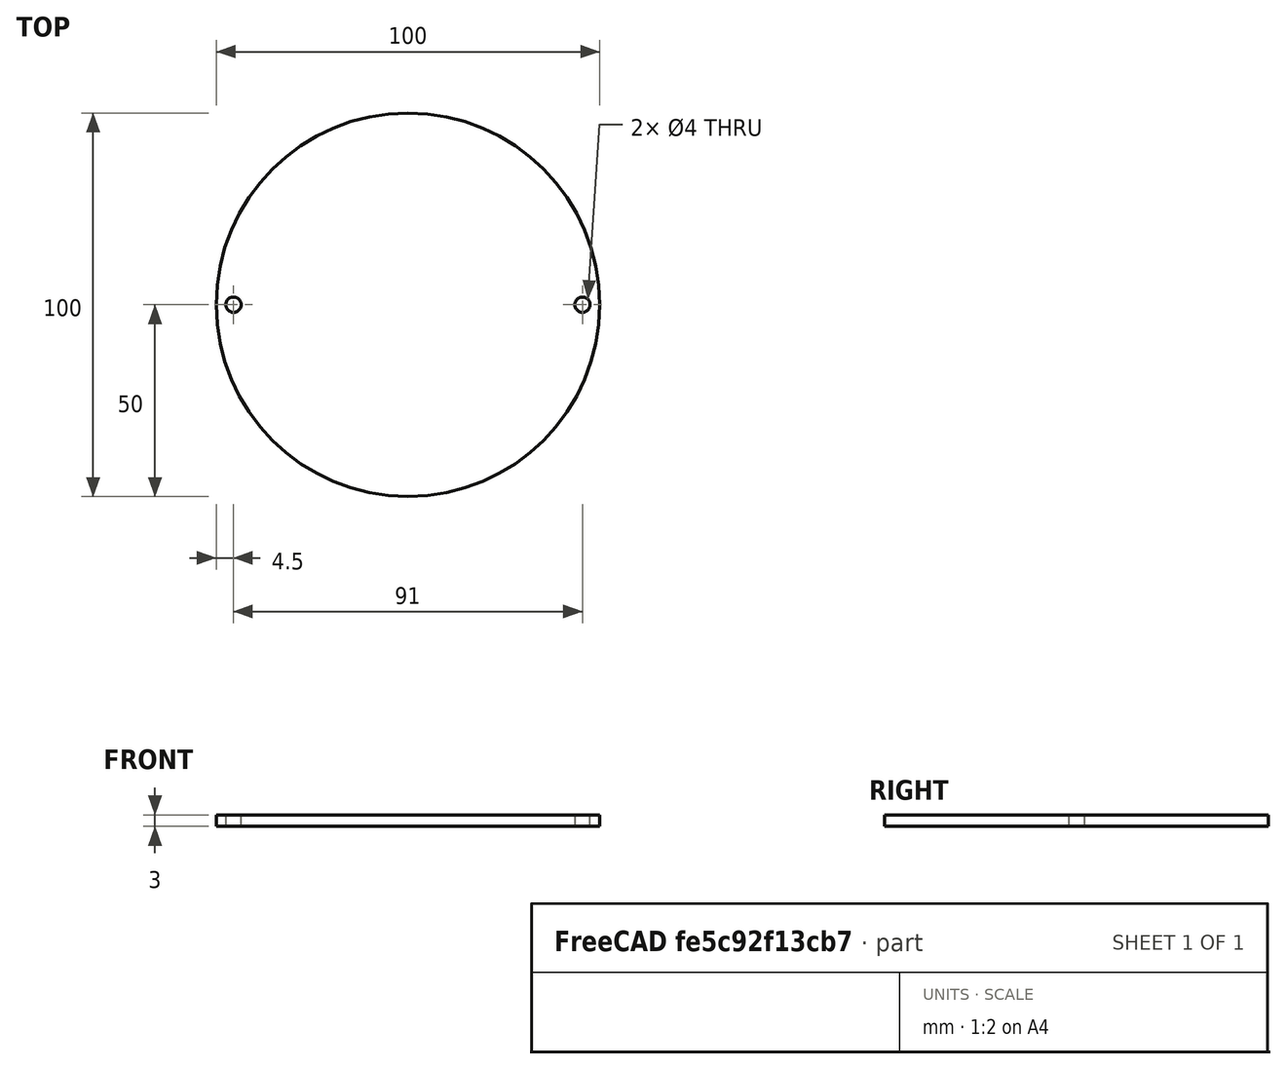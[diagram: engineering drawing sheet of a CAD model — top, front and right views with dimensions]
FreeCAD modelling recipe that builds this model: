
FCSTD DOCUMENT  (FreeCAD 0.20R29410 (Git))
Label: cover_disc_100mm
License: All rights reserved
LicenseURL: http://en.wikipedia.org/wiki/All_rights_reserved
objects: Sketcher::SketchObject×1, PartDesign::Pad×1, PartDesign::Body×1
note: 4 computed .brp shape members not serialized (recipe doc carries the construction recipe); baked Part::Feature solids carry a one-line shape summary decoded from their .brp

FEATURE [Sketcher::SketchObject] Sketch
  FullyConstrained = true
  MapMode = 5
  Support = -> [XY_Plane]
  sketch-geometry (5):
    g0: Circle CenterX=0 CenterY=0 CenterZ=0 NormalX=0 NormalY=0 NormalZ=1 AngleXU=0 Radius=50
    g1: Circle CenterX=-45.5 CenterY=0 CenterZ=0 NormalX=0 NormalY=0 NormalZ=1 AngleXU=0 Radius=2
    g2: Circle CenterX=45.5 CenterY=0 CenterZ=0 NormalX=0 NormalY=0 NormalZ=1 AngleXU=0 Radius=2
    g3: Circle CenterX=0 CenterY=0 CenterZ=0 NormalX=0 NormalY=0 NormalZ=1 AngleXU=0 Radius=45.5
    g4: LineSegment StartX=-50 StartY=0 StartZ=0 EndX=-47.5 EndY=0 EndZ=0
  constraints (14):
    c: Coincident(g0,g-1)
    c: PointOnObject(g1,g-1)
    c: PointOnObject(g2,g-1)
    c: Coincident(g3,g0)
    c: PointOnObject(g1,g3)
    c: PointOnObject(g2,g3)
    c: Equal(g1,g2)
    c: Diameter(g0) = 100  'diameter'
    c: Diameter(g2) = 4  'mounting_hole_diameter'
    c: Horizontal(g4)
    c: PointOnObject(g4,g1)
    c: PointOnObject(g4,g0)
    c: PointOnObject(g4,g-1)
    c: DistanceX(g4,g4) = 2.5
FEATURE [PartDesign::Pad] Pad
  Direction = (0,0,1)
  Length = 3
  Length2 = 10
  Profile = -> Sketch
  ReferenceAxis = -> Sketch [N_Axis]
  Type = 0
FEATURE [PartDesign::Body] Body
  Group = -> [Sketch,Pad]
  Origin = -> Origin
  Tip = -> Pad
